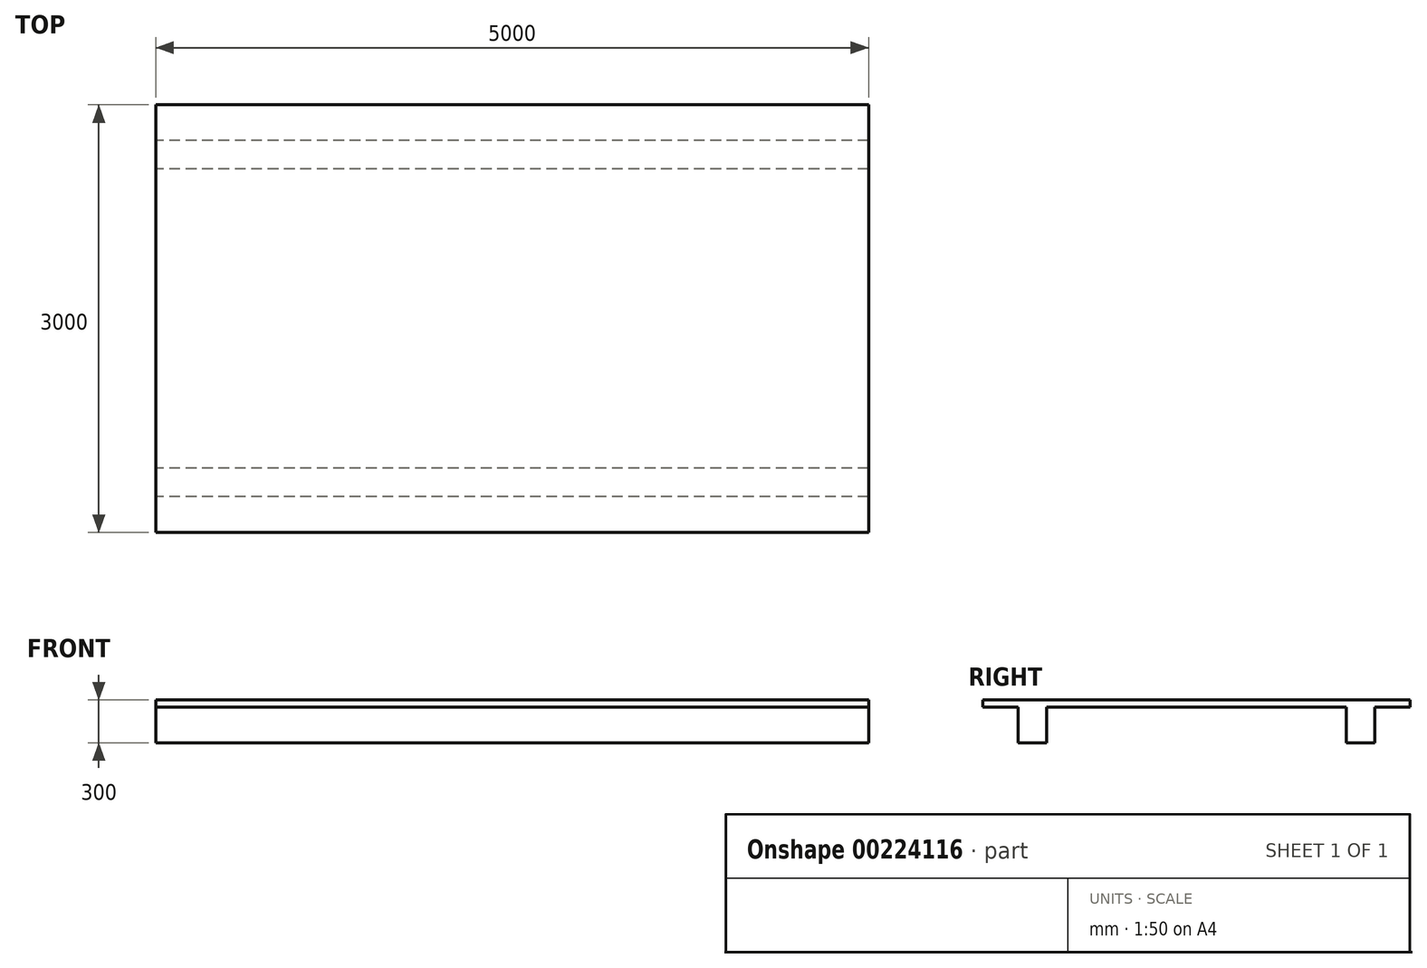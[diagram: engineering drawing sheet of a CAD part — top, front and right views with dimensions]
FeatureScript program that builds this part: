
annotation { "Feature Type Name" : "Feature", "Feature Type Description" : "" }
export const myFeature = defineFeature(function(context is Context, id is Id, definition is map)
    precondition{}
    {
        {
            var Q0;
            Q0=qCreatedBy(makeId("Top.planeOp"),FACE);
            var sketch = newSketch(context, id + "F0", { "sketchPlane" : qUnion([Q0])});
            skLineSegment(sketch, "E0.bottom", {"start": v(0, 0) * mm, "end": v(5000, 0) * mm});
            skLineSegment(sketch, "E0.top", {"start": v(0, -3000) * mm, "end": v(5000, -3000) * mm});
            skLineSegment(sketch, "E0.left", {"start": v(0, 0) * mm, "end": v(0, -3000) * mm});
            skLineSegment(sketch, "E0.right", {"start": v(5000, 0) * mm, "end": v(5000, -3000) * mm});
            skSolve(sketch);
        }
        {
            var Q0;
            Q0 = qSketchRegion(id + "F0", true);
            var Q1;
            Q1=makeQuery(id+"F0.imprint","IMPRINT",FACE,{"disambiguationData":[TD([[makeQuery(id+"F0.imprint","IMPRINT",EDGE,{"derivedFrom":sQuery(id+"F0.wireOp",EDGE,"E0.bottom")}),-1.0]])]});
            extrude(context, id + "F1", {"entities" : qUnion([Q0, Q1]), "depth" : 50 * mm});
        }
        {
            var Q0;
            Q0=makeQuery(id+"F1.opExtrude","CAP_FACE",FACE,{"disambiguationData":[OSD([sQuery(id+"F0.wireOp",EDGE,"E0.bottom"),sQuery(id+"F0.wireOp",EDGE,"E0.top"),sQuery(id+"F0.wireOp",EDGE,"E0.left"),sQuery(id+"F0.wireOp",EDGE,"E0.right")])],"isStart":true});
            var sketch = newSketch(context, id + "F2", { "sketchPlane" : qUnion([Q0])});
            skLineSegment(sketch, "E1.bottom", {"start": v(5000, 2750) * mm, "end": v(0, 2750) * mm});
            skLineSegment(sketch, "E1.top", {"start": v(5000, 2550) * mm, "end": v(0, 2550) * mm});
            skLineSegment(sketch, "E1.left", {"start": v(5000, 2750) * mm, "end": v(5000, 2550) * mm});
            skLineSegment(sketch, "E1.right", {"start": v(0, 2750) * mm, "end": v(0, 2550) * mm});
            skLineSegment(sketch, "E2.bottom", {"start": v(5000, 450) * mm, "end": v(0, 450) * mm});
            skLineSegment(sketch, "E2.top", {"start": v(5000, 250) * mm, "end": v(0, 250) * mm});
            skLineSegment(sketch, "E2.left", {"start": v(5000, 450) * mm, "end": v(5000, 250) * mm});
            skLineSegment(sketch, "E2.right", {"start": v(0, 450) * mm, "end": v(0, 250) * mm});
            skLineSegment(sketch, "E3", {"start": v(0, 250) * mm, "end": v(0, 0) * mm});
            skLineSegment(sketch, "E4", {"start": v(0, 2750) * mm, "end": v(0, 3000) * mm});
            skSolve(sketch);
        }
        {
            var Q0;
            Q0 = qSketchRegion(id + "F2", true);
            extrude(context, id + "F3", {"entities" : qUnion([Q0]), "operationType" : NewBodyOperationType.ADD, "depth" : 250 * mm});
        }
    });
